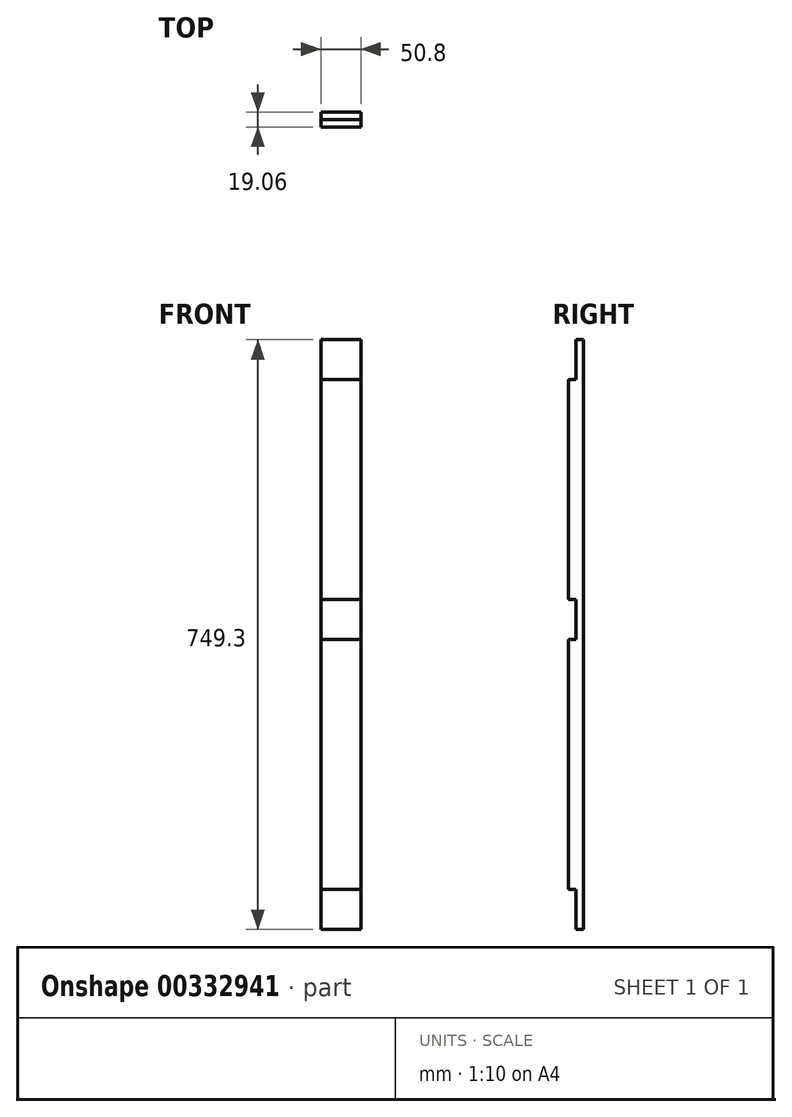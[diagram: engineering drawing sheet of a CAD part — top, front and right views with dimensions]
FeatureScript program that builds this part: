
annotation { "Feature Type Name" : "Feature", "Feature Type Description" : "" }
export const myFeature = defineFeature(function(context is Context, id is Id, definition is map)
    precondition{}
    {
        {
            var Q0;
            Q0=qCreatedBy(makeId("Top.planeOp"),FACE);
            var sketch = newSketch(context, id + "F0", { "sketchPlane" : qUnion([Q0])});
            skLineSegment(sketch, "E0.bottom", {"start": v(25.4, 9.53) * mm, "end": v(-25.4, 9.53) * mm});
            skLineSegment(sketch, "E0.top", {"start": v(25.4, -9.53) * mm, "end": v(-25.4, -9.53) * mm});
            skLineSegment(sketch, "E0.left", {"start": v(25.4, 9.53) * mm, "end": v(25.4, -9.52) * mm});
            skLineSegment(sketch, "E0.right", {"start": v(-25.4, 9.53) * mm, "end": v(-25.4, -9.53) * mm});
            skPoint(sketch, "E0.middle", {"position": v(0, 0) * mm});
            skSolve(sketch);
        }
        {
            var Q0;
            Q0=makeQuery(id+"F0.imprint","IMPRINT",FACE,{"disambiguationData":[TD([[makeQuery(id+"F0.imprint","IMPRINT",EDGE,{"derivedFrom":sQuery(id+"F0.wireOp",EDGE,"E0.bottom")}),1.0]])]});
            extrude(context, id + "F1", {"entities" : qUnion([Q0]), "depth" : 749.3 * mm, "offsetDistance" : 25.4 * mm});
        }
        {
            var Q0;
            Q0=qCreatedBy(makeId("Front.planeOp"),FACE);
            var sketch = newSketch(context, id + "F2", { "sketchPlane" : qUnion([Q0])});
            skLineSegment(sketch, "E1.bottom", {"start": v(-38.77, 0) * mm, "end": v(83.66, 0) * mm});
            skLineSegment(sketch, "E1.top", {"start": v(-38.77, 50.8) * mm, "end": v(83.66, 50.8) * mm});
            skLineSegment(sketch, "E1.left", {"start": v(-38.77, 0) * mm, "end": v(-38.77, 50.8) * mm});
            skLineSegment(sketch, "E1.right", {"start": v(83.66, 0) * mm, "end": v(83.66, 50.8) * mm});
            skLineSegment(sketch, "E2.bottom", {"start": v(-44.21, 368.3) * mm, "end": v(49.65, 368.3) * mm});
            skLineSegment(sketch, "E2.top", {"start": v(-44.21, 419.1) * mm, "end": v(49.65, 419.1) * mm});
            skLineSegment(sketch, "E2.left", {"start": v(-44.21, 368.3) * mm, "end": v(-44.21, 419.1) * mm});
            skLineSegment(sketch, "E2.right", {"start": v(49.65, 368.3) * mm, "end": v(49.65, 419.1) * mm});
            skLineSegment(sketch, "E3.bottom", {"start": v(-210.36, 698.5) * mm, "end": v(132.8, 698.5) * mm});
            skLineSegment(sketch, "E3.top", {"start": v(-210.36, 749.3) * mm, "end": v(132.8, 749.3) * mm});
            skLineSegment(sketch, "E3.left", {"start": v(-210.36, 698.5) * mm, "end": v(-210.36, 749.3) * mm});
            skLineSegment(sketch, "E3.right", {"start": v(132.8, 698.5) * mm, "end": v(132.8, 749.3) * mm});
            skSolve(sketch);
        }
        {
            var Q0;
            Q0=qSketchRegion(id+"F2",true);
            extrude(context, id + "F3", {"entities" : qUnion([Q0]), "operationType" : NewBodyOperationType.REMOVE, "depth" : 25.4 * mm});
        }
    });
